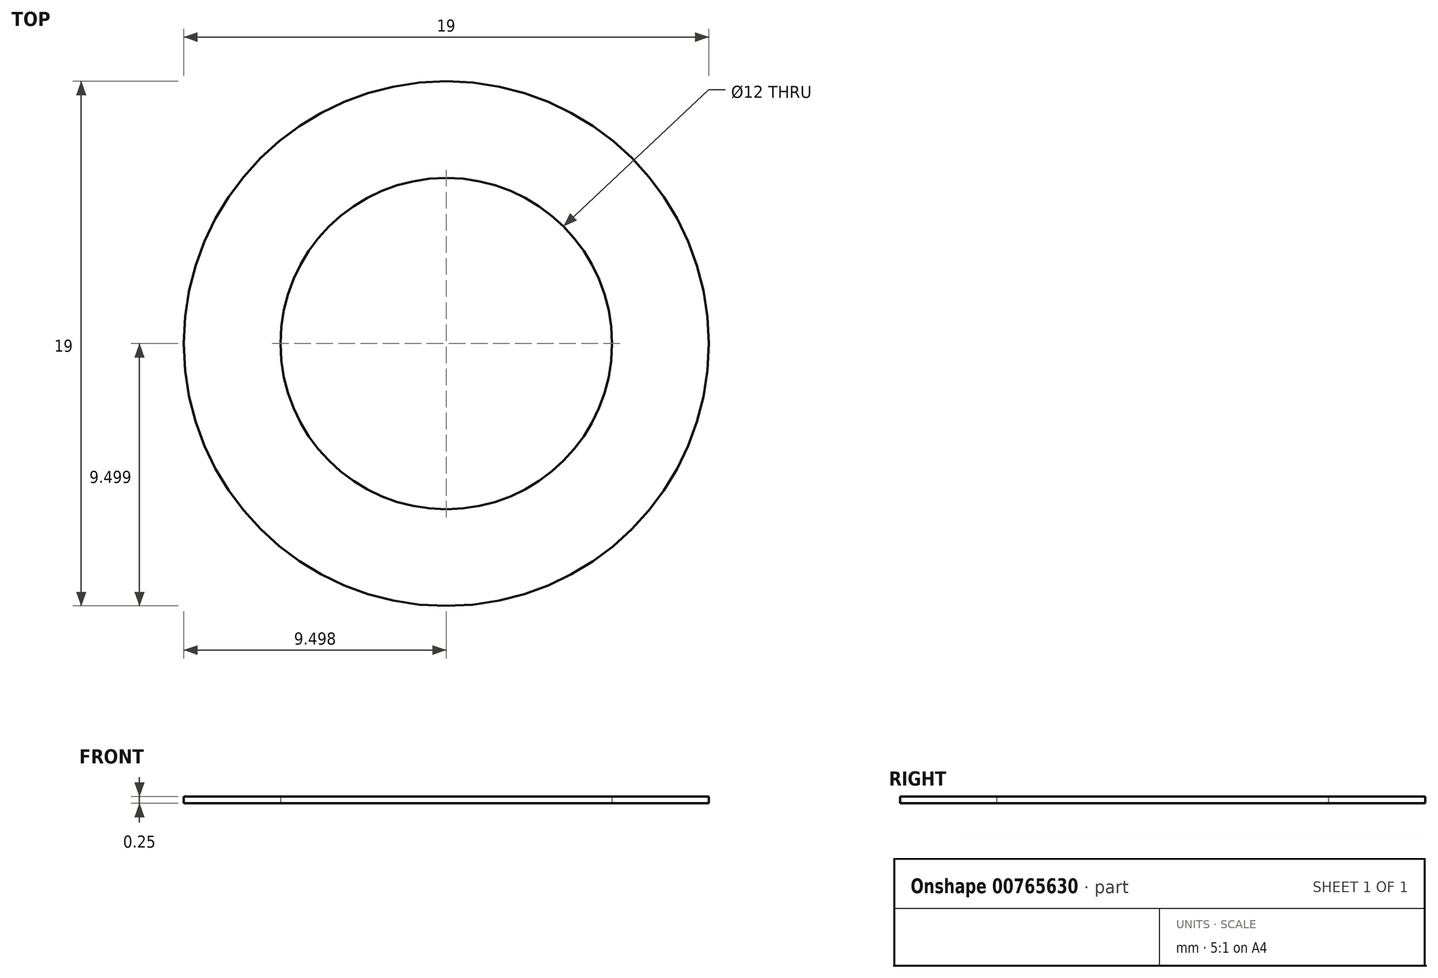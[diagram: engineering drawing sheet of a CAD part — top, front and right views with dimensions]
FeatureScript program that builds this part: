
annotation { "Feature Type Name" : "Feature", "Feature Type Description" : "" }
export const myFeature = defineFeature(function(context is Context, id is Id, definition is map)
    precondition{}
    {
        {
            var Q0;
            Q0=qCreatedBy(makeId("Top.planeOp"),FACE);
            var sketch = newSketch(context, id + "F0", { "sketchPlane" : qUnion([Q0])});
            skLineSegment(sketch, "E0", {"start": v(-5.93, 0.98) * mm, "end": v(-1.93, 0.98) * mm});
            skLineSegment(sketch, "E1", {"start": v(-1.93, 0.98) * mm, "end": v(5.07, 0.98) * mm});
            skLineSegment(sketch, "E2", {"start": v(5.07, 0.98) * mm, "end": v(5.07, -1.03) * mm});
            skLineSegment(sketch, "E3", {"start": v(5.07, -1.03) * mm, "end": v(4.07, -1.03) * mm});
            skLineSegment(sketch, "E4", {"start": v(4.07, -1.03) * mm, "end": v(3.57, -1.03) * mm});
            skLineSegment(sketch, "E5", {"start": v(3.57, -1.03) * mm, "end": v(3.57, 0.98) * mm});
            skLineSegment(sketch, "E6", {"start": v(-1.93, 0.98) * mm, "end": v(-1.93, -1.4) * mm});
            skLineSegment(sketch, "E7", {"start": v(-1.93, -1.4) * mm, "end": v(0.07, -1.4) * mm});
            skLineSegment(sketch, "E8", {"start": v(0.07, -1.4) * mm, "end": v(0.07, 0.98) * mm});
            skCircle(sketch, "E9", {"center": v(-5.93, 0.98) * mm, "radius": 6 * mm});
            skCircle(sketch, "E10", {"center": v(-5.93, 0.98) * mm, "radius": 9.5 * mm});
            skSolve(sketch);
        }
        {
            var Q0;
            {var subQ0=sQuery(id+"F0.wireOp",EDGE,"E8");Q0=makeQuery(id+"F0.imprint","IMPRINT",FACE,{"disambiguationData":[TD([[makeQuery(id+"F0.imprint","IMPRINT",EDGE,{"derivedFrom":subQ0}),-1.0]])]});}
            var Q1;
            {var subQ0=sQuery(id+"F0.wireOp",EDGE,"E8");Q1=makeQuery(id+"F0.imprint","IMPRINT",FACE,{"disambiguationData":[TD([[makeQuery(id+"F0.imprint","IMPRINT",EDGE,{"derivedFrom":subQ0}),1.0]])]});}
            extrude(context, id + "F1", {"entities" : qUnion([Q0, Q1]), "depth" : .25 * mm, "offsetDistance" : 25 * mm});
        }
    });
